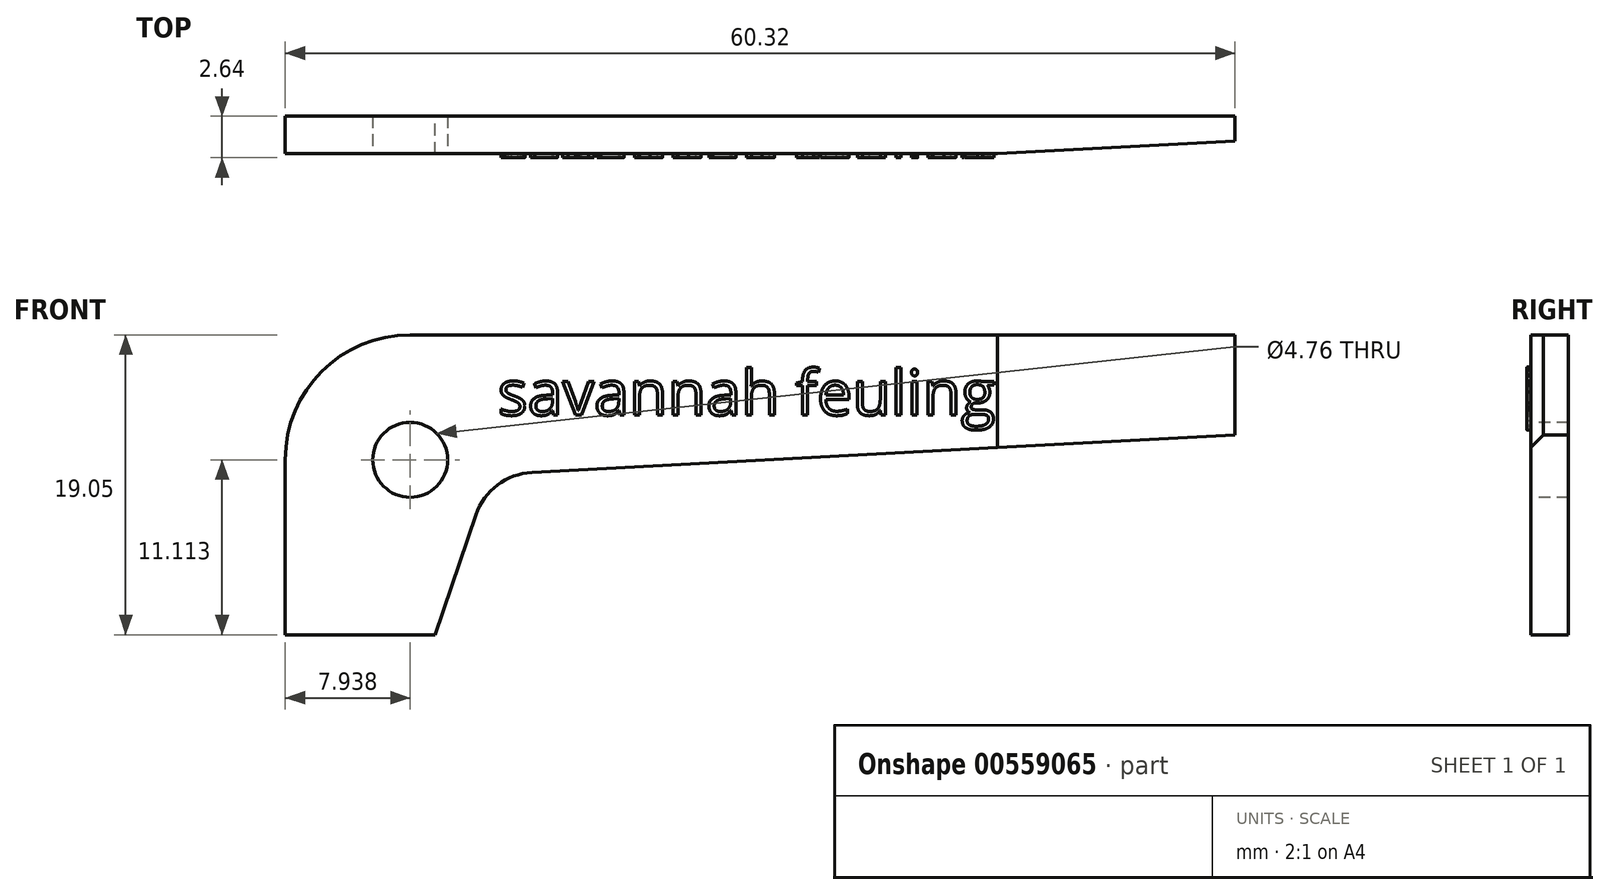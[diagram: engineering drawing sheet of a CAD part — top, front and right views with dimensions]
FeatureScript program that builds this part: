
annotation { "Feature Type Name" : "Feature", "Feature Type Description" : "" }
export const myFeature = defineFeature(function(context is Context, id is Id, definition is map)
    precondition{}
    {
        {
            var Q0;
            Q0=qCreatedBy(makeId("Front.planeOp"),FACE);
            var sketch = newSketch(context, id + "F0", { "sketchPlane" : qUnion([Q0])});
            skLineSegment(sketch, "E0.top", {"start": v(7.94, 19.05) * mm, "end": v(60.33, 19.05) * mm});
            skLineSegment(sketch, "E0.left", {"start": v(0, 0) * mm, "end": v(0, 11.11) * mm});
            skLineSegment(sketch, "E1", {"start": v(9.52, 0) * mm, "end": v(12.12, 7.63) * mm});
            skLineSegment(sketch, "E2", {"start": v(60.33, 12.7) * mm, "end": v(15.66, 10.31) * mm});
            skLineSegment(sketch, "E3", {"start": v(0, 0) * mm, "end": v(9.53, 0) * mm});
            skLineSegment(sketch, "E4", {"start": v(60.33, 19.05) * mm, "end": v(60.33, 12.7) * mm});
            skArc(sketch, "E5", {"start": v(15.66, 10.31) * mm, "mid": v(13.48, 9.51) * mm, "end": v(12.12, 7.63) * mm});
            skPoint(sketch, "E6.visualSharp", {"position": v(0, 19.05) * mm});
            skArc(sketch, "E6.filletArc", {"start": v(7.94, 19.05) * mm, "mid": v(2.32, 16.73) * mm, "end": v(0, 11.11) * mm});
            skSolve(sketch);
        }
        {
            var Q0;
            Q0=makeQuery(id+"F0.imprint","IMPRINT",FACE,{"disambiguationData":[TD([[makeQuery(id+"F0.imprint","IMPRINT",EDGE,{"derivedFrom":sQuery(id+"F0.wireOp",EDGE,"E0.top")}),-1.0]])]});
            extrude(context, id + "F1", {"entities" : qUnion([Q0]), "depth" : 2.38 * mm, "offsetDistance" : 25.4 * mm});
        }
        {
            var Q0;
            Q0=makeQuery(id+"F1.opExtrude","CAP_FACE",FACE,{"disambiguationData":[OSD([sQuery(id+"F0.wireOp",EDGE,"E0.top"),sQuery(id+"F0.wireOp",EDGE,"E0.left"),sQuery(id+"F0.wireOp",EDGE,"E1"),sQuery(id+"F0.wireOp",EDGE,"E2"),sQuery(id+"F0.wireOp",EDGE,"E3"),sQuery(id+"F0.wireOp",EDGE,"E4"),sQuery(id+"F0.wireOp",EDGE,"E5"),sQuery(id+"F0.wireOp",EDGE,"E6.filletArc")])],"isStart":false});
            var sketch = newSketch(context, id + "F2", { "sketchPlane" : qUnion([Q0])});
            skCircle(sketch, "E7", {"center": v(7.94, 11.11) * mm, "radius": 2.38 * mm});
            skSolve(sketch);
        }
        {
            var Q0;
            Q0=makeQuery(id+"F2.imprint","IMPRINT",FACE,{"disambiguationData":[TD([[makeQuery(id+"F2.imprint","IMPRINT",EDGE,{"derivedFrom":sQuery(id+"F2.wireOp",EDGE,"E7")}),1.0]])]});
            extrude(context, id + "F3", {"entities" : qUnion([Q0]), "operationType" : NewBodyOperationType.REMOVE, "endBound" : BoundingType.THROUGH_ALL, "oppositeDirection" : true, "depth" : 25.4 * mm, "offsetDistance" : 25.4 * mm});
        }
        {
            var Q0;
            Q0=makeQuery(id+"F1.opExtrude","SWEPT_FACE",FACE,{"disambiguationData":[OSD([sQuery(id+"F0.wireOp",EDGE,"E0.top")])]});
            var sketch = newSketch(context, id + "F4", { "sketchPlane" : qUnion([Q0])});
            skLineSegment(sketch, "E8", {"start": v(45.24, 0) * mm, "end": v(60.33, -0.8) * mm});
            skLineSegment(sketch, "E9", {"start": v(60.33, -0.8) * mm, "end": v(45.24, 0) * mm});
            skLineSegment(sketch, "E10.MirrorCS", {"start": v(60.33, -1.59) * mm, "end": v(45.24, -2.38) * mm});
            skSolve(sketch);
        }
        {
            var Q0;
            {var subQ0=sQuery(id+"F4.wireOp",EDGE,"E10.MirrorCS");Q0=makeQuery(id+"F4.imprint","IMPRINT",FACE,{"disambiguationData":[TD([[makeQuery(id+"F4.imprint","IMPRINT",EDGE,{"derivedFrom":subQ0}),1.0]])]});}
            var Q1;
            {var subQ0=sQuery(id+"F4.wireOp",EDGE,"E9");Q1=makeQuery(id+"F4.imprint","IMPRINT",FACE,{"disambiguationData":[TD([[makeQuery(id+"F4.imprint","IMPRINT",EDGE,{"derivedFrom":subQ0}),-1.0]])]});}
            extrude(context, id + "F5", {"entities" : qUnion([Q0, Q1]), "operationType" : NewBodyOperationType.REMOVE, "oppositeDirection" : true, "depth" : 25.4 * mm, "offsetDistance" : 25.4 * mm});
        }
        {
            var Q0;
            Q0=makeQuery(id+"F1.opExtrude","CAP_FACE",FACE,{"disambiguationData":[OSD([sQuery(id+"F0.wireOp",EDGE,"E0.top"),sQuery(id+"F0.wireOp",EDGE,"E0.left"),sQuery(id+"F0.wireOp",EDGE,"E1"),sQuery(id+"F0.wireOp",EDGE,"E2"),sQuery(id+"F0.wireOp",EDGE,"E3"),sQuery(id+"F0.wireOp",EDGE,"E4"),sQuery(id+"F0.wireOp",EDGE,"E5"),sQuery(id+"F0.wireOp",EDGE,"E6.filletArc")])],"isStart":false});
            var sketch = newSketch(context, id + "F6", { "sketchPlane" : qUnion([Q0])});
            skText(sketch, "E11", { "text": "savannah feuling\n", "fontName": "OpenSans-Regular.ttf"});
            const initialGuessF6  = {"E11": [0.0135, 0.01395, 1, 0, 0.00287]};
            skSetInitialGuess(sketch, initialGuessF6);
            skSolve(sketch);
        }
        {
            var Q0;
            Q0 = qSketchRegion(id + "F6", true);
            extrude(context, id + "F7", {"entities" : qUnion([Q0]), "operationType" : NewBodyOperationType.ADD, "depth" : 0.25 * mm, "offsetDistance" : 25.4 * mm});
        }
    });
